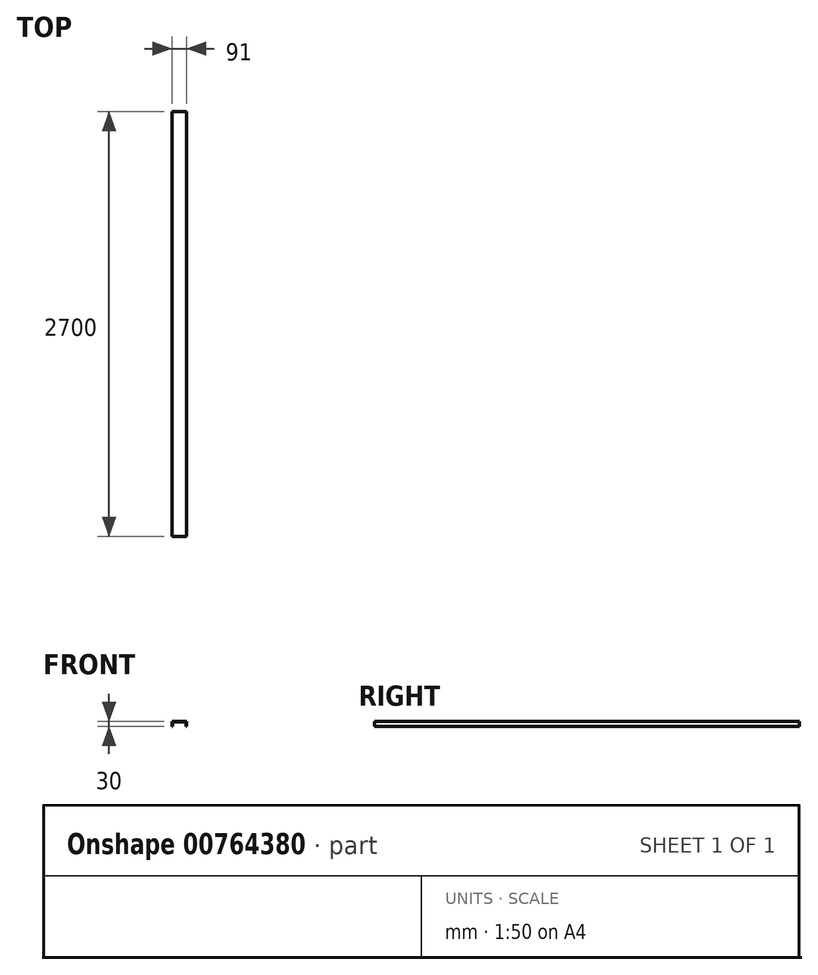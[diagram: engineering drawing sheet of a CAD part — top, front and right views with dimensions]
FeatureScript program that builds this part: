
annotation { "Feature Type Name" : "Feature", "Feature Type Description" : "" }
export const myFeature = defineFeature(function(context is Context, id is Id, definition is map)
    precondition{}
    {
        {
            var Q0;
            Q0=qCreatedBy(makeId("Front.planeOp"),FACE);
            var sketch = newSketch(context, id + "F0", { "sketchPlane" : qUnion([Q0])});
            skLineSegment(sketch, "E0", {"start": v(0, 30) * mm, "end": v(45.5, 30) * mm});
            skLineSegment(sketch, "E1", {"start": v(45.5, 30) * mm, "end": v(45.5, 0) * mm});
            skLineSegment(sketch, "E2", {"start": v(0, 30) * mm, "end": v(-45.5, 30) * mm});
            skLineSegment(sketch, "E3", {"start": v(-45.5, 30) * mm, "end": v(-45.5, 0) * mm});
            skLineSegment(sketch, "E4.0", {"start": v(-42.5, 27) * mm, "end": v(-42.5, 0) * mm});
            skLineSegment(sketch, "E4.1", {"start": v(0, 27) * mm, "end": v(-42.5, 27) * mm});
            skLineSegment(sketch, "E4.2", {"start": v(0, 27) * mm, "end": v(42.5, 27) * mm});
            skLineSegment(sketch, "E4.3", {"start": v(42.5, 27) * mm, "end": v(42.5, 0) * mm});
            skLineSegment(sketch, "E5", {"start": v(-45.5, 0) * mm, "end": v(-42.5, 0) * mm});
            skLineSegment(sketch, "E6", {"start": v(42.5, 0) * mm, "end": v(45.5, 0) * mm});
            skSolve(sketch);
        }
        {
            var Q0;
            Q0=makeQuery(id+"F0.imprint","IMPRINT",FACE,{"disambiguationData":[TD([[makeQuery(id+"F0.imprint","IMPRINT",EDGE,{"derivedFrom":sQuery(id+"F0.wireOp",EDGE,"E0")}),-1.0]])]});
            extrude(context, id + "F1", {"entities" : qUnion([Q0]), "depth" : 2700 * mm, "offsetDistance" : 25 * mm, "symmetric" : true});
        }
    });
